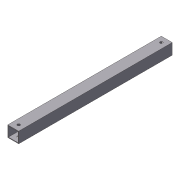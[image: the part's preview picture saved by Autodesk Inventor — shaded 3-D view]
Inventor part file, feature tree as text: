
AUTODESK INVENTOR PART (.ipt)
format: ipt  version: 2012 (Build 160160000, 160)  size: 86,528 bytes
history: native  units: in
note: dims shown in document units (in); Inventor stores cm internally (conversion verified against a paired STEP export)
features: extrude x2, sketch x2, shell x1
ambient origin geometry x8: Origin, YZ Plane, XZ Plane, XY Plane, X Axis, Y Axis, Z Axis, Center Point
bodies: Solid1 (feature_tree)
feature tree (5):
  extrude  "Extrusion1"  Depth=1.0in
  shell  "Shell1"  Thickness=14.0in
  extrude  "Extrusion2"  Depth=0.25in
  sketch  "Sketch1"  dims[d0=1.0in d1=1.0in d2=14.0in d3=0.0in]
  sketch  "Sketch2"  dims[d4=0.0625in d5=0.25in d6=0.5in d7=0.5in d8=0.5in d9=0.5in d10=13.0in d11=0.0in]
